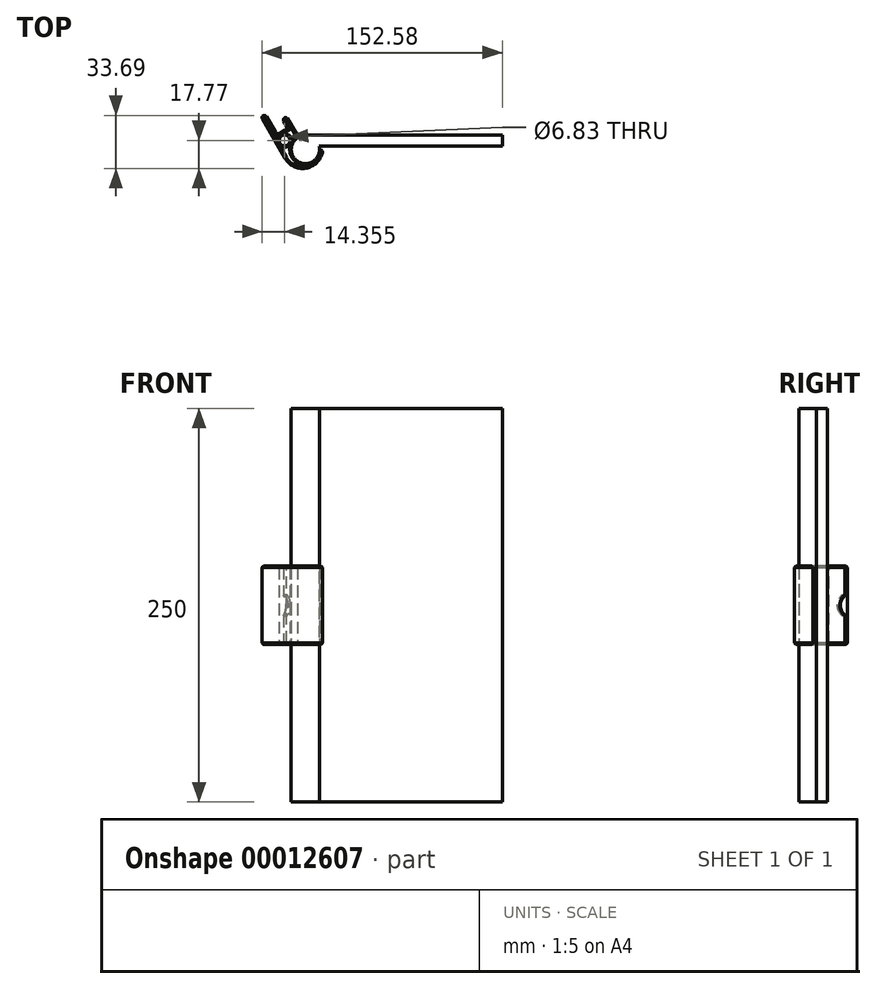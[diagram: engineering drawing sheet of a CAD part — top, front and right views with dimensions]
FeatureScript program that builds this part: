
annotation { "Feature Type Name" : "Feature", "Feature Type Description" : "" }
export const myFeature = defineFeature(function(context is Context, id is Id, definition is map)
    precondition{}
    {
        {
            var Q0;
            Q0=qCreatedBy(makeId("Top.planeOp"),FACE);
            var sketch = newSketch(context, id + "F0", { "sketchPlane" : qUnion([Q0])});
            skArc(sketch, "E0", {"start": v(9, 0) * mm, "mid": v(-4.5, -7.8) * mm, "end": v(-4.5, 7.8) * mm});
            skLineSegment(sketch, "E1", {"start": v(0, 0) * mm, "end": v(22.7, 0) * mm, "construction": true});
            skLineSegment(sketch, "E2", {"start": v(0, 0) * mm, "end": v(-19.43, 33.65) * mm, "construction": true});
            skLineSegment(sketch, "E3", {"start": v(9, 0) * mm, "end": v(11, 0) * mm});
            skLineSegment(sketch, "E4", {"start": v(-12.92, -5.61) * mm, "end": v(-28.12, 20.71) * mm});
            skLineSegment(sketch, "E5", {"start": v(-28.12, 20.71) * mm, "end": v(-25.53, 22.21) * mm});
            skLineSegment(sketch, "E6", {"start": v(-25.53, 22.21) * mm, "end": v(-18.03, 9.22) * mm});
            skLineSegment(sketch, "E7", {"start": v(-18.03, 9.22) * mm, "end": v(-11.1, 13.22) * mm});
            skLineSegment(sketch, "E8", {"start": v(-11.1, 13.22) * mm, "end": v(-14.6, 19.28) * mm});
            skLineSegment(sketch, "E9", {"start": v(-14.6, 19.28) * mm, "end": v(-12, 20.78) * mm});
            skArc(sketch, "E10", {"start": v(-12.92, -5.61) * mm, "mid": v(1.12, -11.7) * mm, "end": v(11, 0) * mm});
            skLineSegment(sketch, "E11", {"start": v(40.86, 23.59) * mm, "end": v(-39.8, -22.98) * mm, "construction": true});
            skLineSegment(sketch, "E12", {"start": v(-12, 20.78) * mm, "end": v(-4.5, 7.8) * mm});
            skCircle(sketch, "E13", {"center": v(-13.22, 5.74) * mm, "radius": 3.42 * mm});
            skSolve(sketch);
        }
        {
            var Q0;
            Q0=qSketchRegion(id+"F0",true);
            extrude(context, id + "F1", {"entities" : qUnion([Q0]), "depth" : 50 * mm, "symmetric" : true});
        }
        {
            var Q0;
            Q0=makeQuery(id+"F1.opExtrude","SWEPT_EDGE",EDGE,{"disambiguationData":[OSD([sQuery(id+"F0.wireOp",EDGE,"E5"),sQuery(id+"F0.wireOp",EDGE,"E6")])]});
            var Q1;
            Q1=makeQuery(id+"F1.opExtrude","SWEPT_EDGE",EDGE,{"disambiguationData":[OSD([sQuery(id+"F0.wireOp",EDGE,"E4"),sQuery(id+"F0.wireOp",EDGE,"E5")])]});
            var Q2;
            Q2=makeQuery(id+"F1.opExtrude","SWEPT_EDGE",EDGE,{"disambiguationData":[OSD([sQuery(id+"F0.wireOp",EDGE,"E8"),sQuery(id+"F0.wireOp",EDGE,"E9")])]});
            var Q3;
            Q3=makeQuery(id+"F1.opExtrude","SWEPT_EDGE",EDGE,{"disambiguationData":[OSD([sQuery(id+"F0.wireOp",EDGE,"E9"),sQuery(id+"F0.wireOp",EDGE,"E12")])]});
            var Q4;
            Q4=makeQuery(id+"F1.opExtrude","SWEPT_EDGE",EDGE,{"disambiguationData":[OSD([sQuery(id+"F0.wireOp",EDGE,"E0"),sQuery(id+"F0.wireOp",EDGE,"E3")])]});
            var Q5;
            Q5=makeQuery(id+"F1.opExtrude","SWEPT_EDGE",EDGE,{"disambiguationData":[OSD([sQuery(id+"F0.wireOp",EDGE,"E3"),sQuery(id+"F0.wireOp",EDGE,"E10")])]});
            fillet(context, id + "F2", {"entities" : qUnion([Q0, Q1, Q2, Q3, Q4, Q5]), "radius" : 1.5 * mm, "tangentPropagation" : true, "allowEdgeOverflow" : false});
        }
        {
            var Q0;
            Q0=makeQuery(id+"F1.opExtrude","SWEPT_EDGE",EDGE,{"disambiguationData":[OSD([sQuery(id+"F0.wireOp",EDGE,"E0"),sQuery(id+"F0.wireOp",EDGE,"E12")])]});
            fillet(context, id + "F3", {"entities" : qUnion([Q0]), "radius" : 2 * mm, "tangentPropagation" : true, "allowEdgeOverflow" : false});
        }
        {
            var Q0;
            Q0=makeQuery(id+"F1.opExtrude","SWEPT_FACE",FACE,{"disambiguationData":[OSD([sQuery(id+"F0.wireOp",EDGE,"E12")])]});
            var sketch = newSketch(context, id + "F4", { "sketchPlane" : qUnion([Q0])});
            skCircle(sketch, "E14", {"center": v(27.5, 0) * mm, "radius": 7 * mm});
            skPoint(sketch, "E15", {"position": v(10.82, 0) * mm});
            skPoint(sketch, "E16", {"position": v(22.5, 0) * mm});
            skSolve(sketch);
        }
        {
            var Q0;
            Q0=qSketchRegion(id+"F4",true);
            var Q1;
            Q1=makeQuery(id+"F1.opExtrude","SWEPT_FACE",FACE,{"disambiguationData":[OSD([sQuery(id+"F0.wireOp",EDGE,"E8")])]});
            extrude(context, id + "F5", {"entities" : qUnion([Q0]), "operationType" : NewBodyOperationType.REMOVE, "endBound" : BoundingType.UP_TO_SURFACE, "oppositeDirection" : true, "endBoundEntityFace" : qUnion([Q1]), "depth" : 25 * mm});
        }
        {
            var Q0;
            Q0=makeQuery(id+"F1.opExtrude","CAP_FACE",FACE,{"disambiguationData":[OSD([sQuery(id+"F0.wireOp",EDGE,"E0"),sQuery(id+"F0.wireOp",EDGE,"E3"),sQuery(id+"F0.wireOp",EDGE,"E4"),sQuery(id+"F0.wireOp",EDGE,"E5"),sQuery(id+"F0.wireOp",EDGE,"E6"),sQuery(id+"F0.wireOp",EDGE,"E7"),sQuery(id+"F0.wireOp",EDGE,"E8"),sQuery(id+"F0.wireOp",EDGE,"E9"),sQuery(id+"F0.wireOp",EDGE,"E10"),sQuery(id+"F0.wireOp",EDGE,"E12")])],"isStart":false});
            var Q1;
            Q1=makeQuery(id+"F1.opExtrude","CAP_FACE",FACE,{"disambiguationData":[OSD([sQuery(id+"F0.wireOp",EDGE,"E0"),sQuery(id+"F0.wireOp",EDGE,"E3"),sQuery(id+"F0.wireOp",EDGE,"E4"),sQuery(id+"F0.wireOp",EDGE,"E5"),sQuery(id+"F0.wireOp",EDGE,"E6"),sQuery(id+"F0.wireOp",EDGE,"E7"),sQuery(id+"F0.wireOp",EDGE,"E8"),sQuery(id+"F0.wireOp",EDGE,"E9"),sQuery(id+"F0.wireOp",EDGE,"E10"),sQuery(id+"F0.wireOp",EDGE,"E12")])],"isStart":true});
            chamfer(context, id + "F6", {"entities" : qUnion([Q0, Q1]), "width" : 0.95 * mm, "tangentPropagation" : true});
        }
        {
            var Q0;
            Q0=makeQuery(id+"F1.opExtrude","SWEPT_EDGE",EDGE,{"disambiguationData":[OSD([sQuery(id+"F0.wireOp",EDGE,"E6"),sQuery(id+"F0.wireOp",EDGE,"E7")])]});
            var Q1;
            Q1=makeQuery(id+"F1.opExtrude","SWEPT_EDGE",EDGE,{"disambiguationData":[OSD([sQuery(id+"F0.wireOp",EDGE,"E7"),sQuery(id+"F0.wireOp",EDGE,"E8")])]});
            fillet(context, id + "F7", {"entities" : qUnion([Q0, Q1]), "radius" : 2 * mm, "tangentPropagation" : true, "allowEdgeOverflow" : false});
        }
        {
            var Q0;
            Q0=qCreatedBy(makeId("Top.planeOp"),FACE);
            var sketch = newSketch(context, id + "F8", { "sketchPlane" : qUnion([Q0])});
            skCircle(sketch, "E17", {"center": v(0, 0) * mm, "radius": 9 * mm});
            skLineSegment(sketch, "E18.bottom", {"start": v(0, 9) * mm, "end": v(125, 9) * mm});
            skLineSegment(sketch, "E18.top", {"start": v(0, 2.14) * mm, "end": v(125, 2.14) * mm});
            skLineSegment(sketch, "E18.left", {"start": v(0, 9) * mm, "end": v(0, 2.14) * mm});
            skLineSegment(sketch, "E18.right", {"start": v(125, 9) * mm, "end": v(125, 2.14) * mm});
            skLineSegment(sketch, "E19", {"start": v(-32.62, 38.23) * mm, "end": v(28.74, -33.68) * mm, "construction": true});
            skSolve(sketch);
        }
        {
            var Q0;
            Q0=qSketchRegion(id+"F8",true);
            extrude(context, id + "F9", {"entities" : qUnion([Q0]), "depth" : 250 * mm, "symmetric" : true});
        }
        {
            var Q0;
            Q0=makeQuery(id+"F5.boolean.opBoolean","COPY",FACE,{"derivedFrom":makeQuery(id+"F5.opExtrude","SWEPT_FACE",FACE,{"disambiguationData":[OSD([sQuery(id+"F4.wireOp",EDGE,"E14")])]})});
            chamfer(context, id + "F10", {"entities" : qUnion([Q0]), "width" : 1 * mm, "tangentPropagation" : true});
        }
    });
